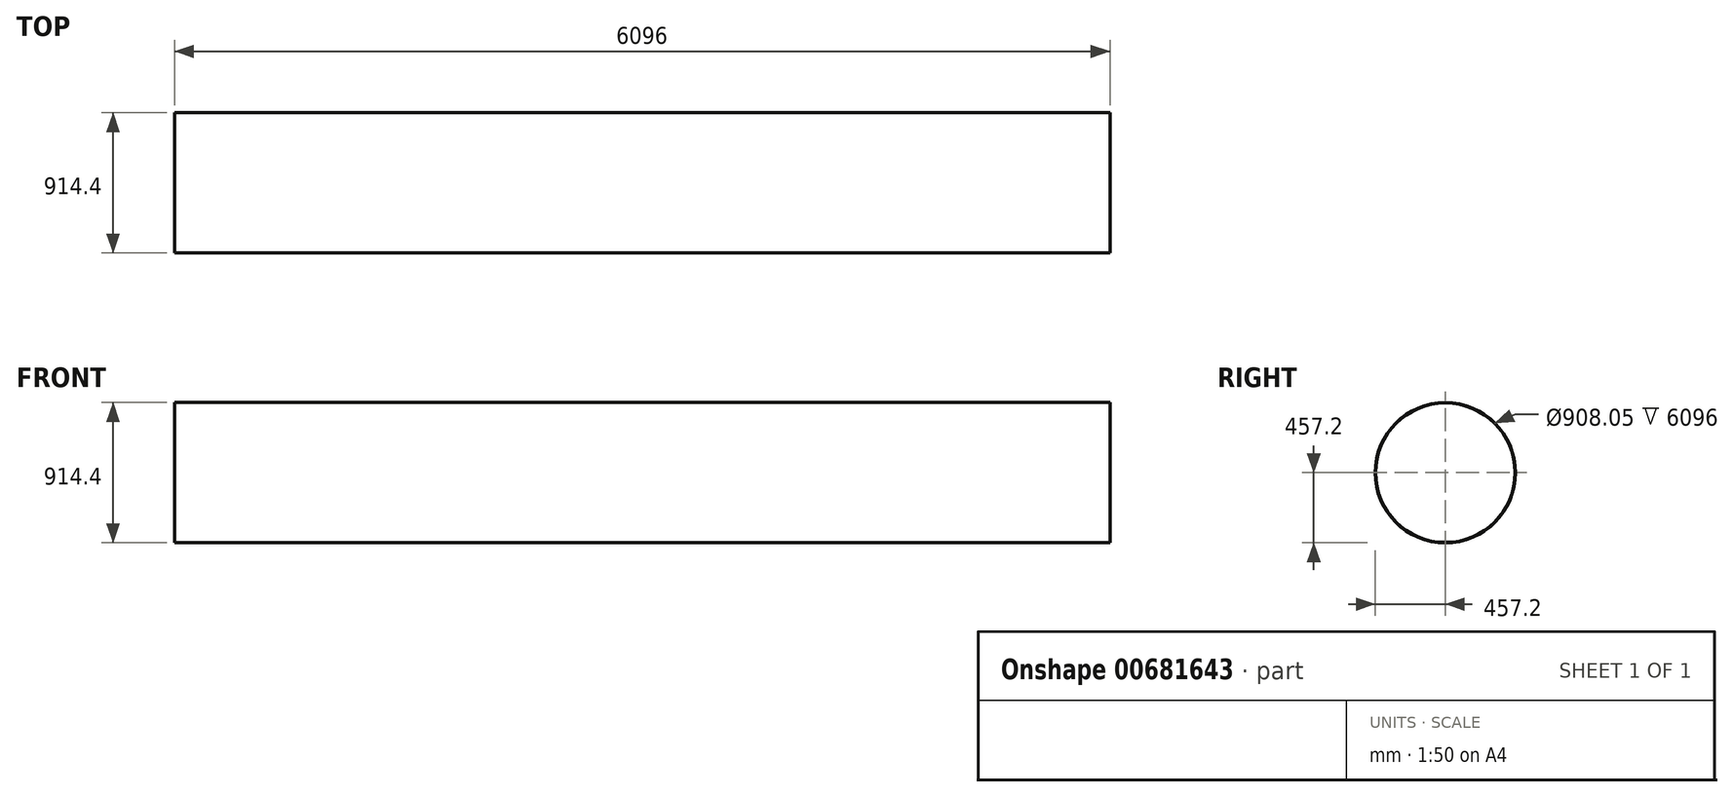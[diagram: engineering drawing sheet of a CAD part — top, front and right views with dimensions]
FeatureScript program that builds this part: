
annotation { "Feature Type Name" : "Feature", "Feature Type Description" : "" }
export const myFeature = defineFeature(function(context is Context, id is Id, definition is map)
    precondition{}
    {
        {
            var Q0;
            Q0=qCreatedBy(makeId("Right.planeOp"),FACE);
            var sketch = newSketch(context, id + "F0", { "sketchPlane" : qUnion([Q0])});
            skCircle(sketch, "E0", {"center": v(0, 0) * mm, "radius": 457.2 * mm});
            skCircle(sketch, "E1", {"center": v(0, 0) * mm, "radius": 454.03 * mm});
            skSolve(sketch);
        }
        {
            var Q0;
            Q0=makeQuery(id+"F0.imprint","IMPRINT",FACE,{"disambiguationData":[TD([[makeQuery(id+"F0.imprint","IMPRINT",EDGE,{"derivedFrom":sQuery(id+"F0.wireOp",EDGE,"E0")}),1.0]])]});
            extrude(context, id + "F1", {"entities" : qUnion([Q0]), "depth" : 6096 * mm, "offsetDistance" : 25.4 * mm});
        }
    });
